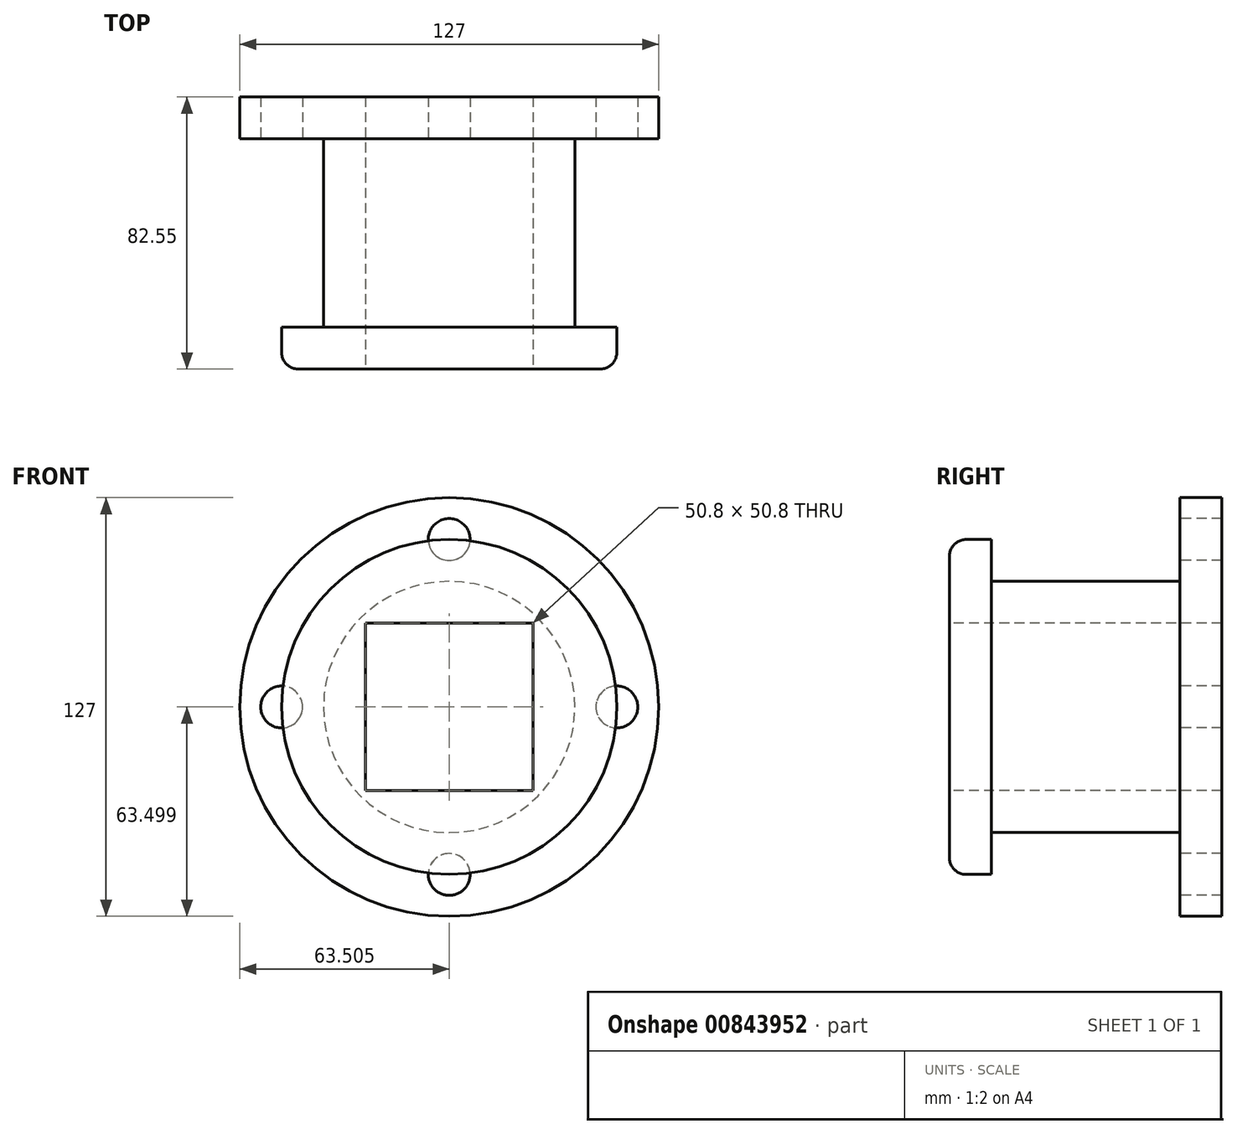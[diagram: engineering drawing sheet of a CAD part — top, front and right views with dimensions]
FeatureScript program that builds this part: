
annotation { "Feature Type Name" : "Feature", "Feature Type Description" : "" }
export const myFeature = defineFeature(function(context is Context, id is Id, definition is map)
    precondition{}
    {
        {
            var Q0;
            Q0=qCreatedBy(makeId("Front.planeOp"),FACE);
            var sketch = newSketch(context, id + "F0", { "sketchPlane" : qUnion([Q0])});
            skCircle(sketch, "E0", {"center": v(-41.54, 15.85) * mm, "radius": 63.5 * mm});
            skSolve(sketch);
        }
        {
            var Q0;
            Q0 = qSketchRegion(id + "F0", true);
            extrude(context, id + "F1", {"entities" : qUnion([Q0]), "depth" : 12.7 * mm, "offsetDistance" : 25.4 * mm});
        }
        {
            var Q0;
            Q0=makeQuery(id+"F1.opExtrude","CAP_FACE",FACE,{"disambiguationData":[OSD([sQuery(id+"F0.wireOp",EDGE,"E0")])],"isStart":false});
            var sketch = newSketch(context, id + "F2", { "sketchPlane" : qUnion([Q0])});
            skCircle(sketch, "E1", {"center": v(-41.54, 66.65) * mm, "radius": 6.35 * mm});
            skCircle(sketch, "E2", {"center": v(-41.54, -34.95) * mm, "radius": 6.35 * mm});
            skCircle(sketch, "E3", {"center": v(9.26, 15.85) * mm, "radius": 6.35 * mm});
            skCircle(sketch, "E4", {"center": v(-92.34, 15.85) * mm, "radius": 6.35 * mm});
            skPoint(sketch, "E5.center.orphan", {"position": v(-41.54, 15.85) * mm});
            skSolve(sketch);
        }
        {
            var Q0;
            Q0 = qSketchRegion(id + "F2", true);
            extrude(context, id + "F3", {"entities" : qUnion([Q0]), "operationType" : NewBodyOperationType.REMOVE, "oppositeDirection" : true, "depth" : 12.7 * mm, "offsetDistance" : 25.4 * mm});
        }
        {
            var Q0;
            Q0=makeQuery(id+"F1.opExtrude","CAP_FACE",FACE,{"disambiguationData":[OSD([sQuery(id+"F0.wireOp",EDGE,"E0")])],"isStart":false});
            var sketch = newSketch(context, id + "F4", { "sketchPlane" : qUnion([Q0])});
            skCircle(sketch, "E6", {"center": v(-41.54, 15.85) * mm, "radius": 38.1 * mm});
            skSolve(sketch);
        }
        {
            var Q0;
            Q0 = qSketchRegion(id + "F4", true);
            extrude(context, id + "F5", {"entities" : qUnion([Q0]), "operationType" : NewBodyOperationType.ADD, "depth" : 57.15 * mm, "offsetDistance" : 25.4 * mm});
        }
        {
            var Q0;
            Q0=makeQuery(id+"F5.opExtrude","CAP_FACE",FACE,{"disambiguationData":[OSD([sQuery(id+"F4.wireOp",EDGE,"E6")])],"isStart":false});
            var sketch = newSketch(context, id + "F6", { "sketchPlane" : qUnion([Q0])});
            skCircle(sketch, "E7", {"center": v(-41.54, 15.85) * mm, "radius": 50.8 * mm});
            skSolve(sketch);
        }
        {
            var Q0;
            Q0 = qSketchRegion(id + "F6", true);
            extrude(context, id + "F7", {"entities" : qUnion([Q0]), "operationType" : NewBodyOperationType.ADD, "depth" : 12.7 * mm, "offsetDistance" : 25.4 * mm});
        }
        {
            var Q0;
            Q0=makeQuery(id+"F7.opExtrude","CAP_FACE",FACE,{"disambiguationData":[OSD([sQuery(id+"F6.wireOp",EDGE,"E7")])],"isStart":false});
            var sketch = newSketch(context, id + "F8", { "sketchPlane" : qUnion([Q0])});
            skLineSegment(sketch, "E8.bottom", {"start": v(-16.14, 41.25) * mm, "end": v(-66.94, 41.25) * mm});
            skLineSegment(sketch, "E8.top", {"start": v(-16.14, -9.55) * mm, "end": v(-66.94, -9.55) * mm});
            skLineSegment(sketch, "E8.left", {"start": v(-16.14, 41.25) * mm, "end": v(-16.14, -9.55) * mm});
            skLineSegment(sketch, "E8.right", {"start": v(-66.94, 41.25) * mm, "end": v(-66.94, -9.55) * mm});
            skPoint(sketch, "E8.middle", {"position": v(-41.54, 15.85) * mm});
            skSolve(sketch);
        }
        {
            var Q0;
            Q0 = qSketchRegion(id + "F8", true);
            extrude(context, id + "F9", {"entities" : qUnion([Q0]), "operationType" : NewBodyOperationType.REMOVE, "oppositeDirection" : true, "depth" : 101.6 * mm, "offsetDistance" : 25.4 * mm});
        }
        {
            var Q0;
            Q0=makeQuery(id+"F7.opExtrude","CAP_EDGE",EDGE,{"disambiguationData":[OSD([sQuery(id+"F6.wireOp",EDGE,"E7")])],"isStart":false});
            fillet(context, id + "F10", {"entities" : qUnion([Q0]), "radius" : 5.08 * mm, "tangentPropagation" : true, "allowEdgeOverflow" : false});
        }
    });
